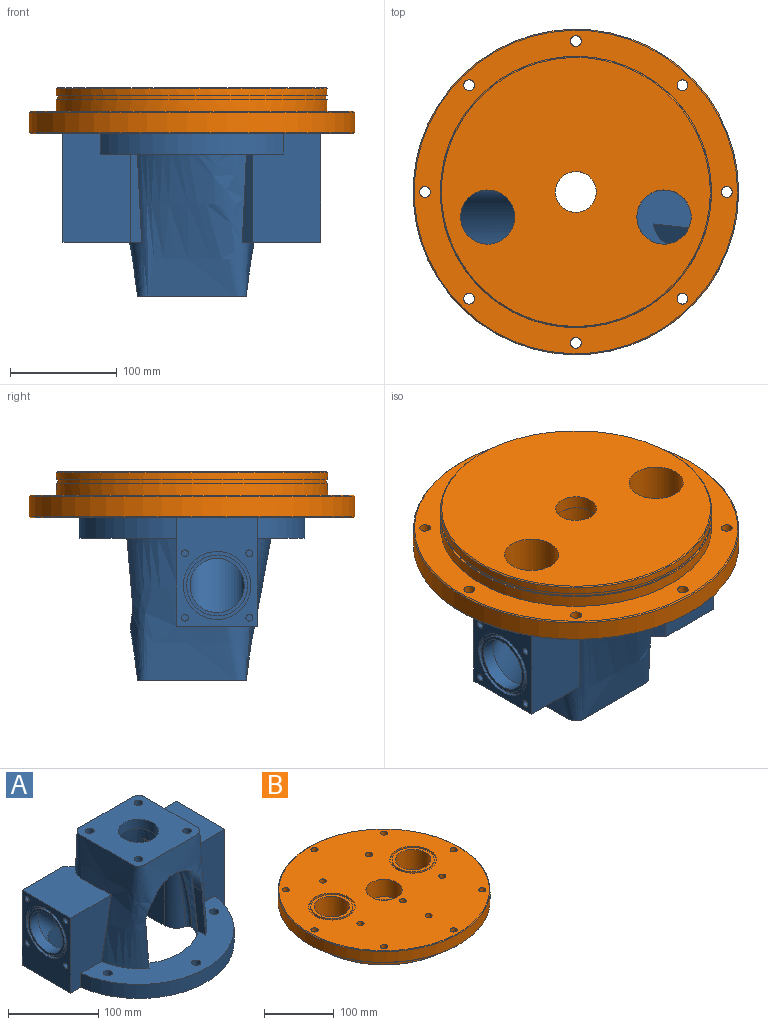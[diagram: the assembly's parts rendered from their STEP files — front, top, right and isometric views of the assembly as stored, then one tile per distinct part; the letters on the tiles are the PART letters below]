
ASSEMBLY  parts=2 mates=1
PART A: 80 faces, bbox 288x215.9x173.7 mm
  f0: plane 57.15x57.15mm, normal (-1,0,0), area 538.4mm2, adj f35,f61
  f1: plane 57.15x57.15mm, normal (1,0,0), area 538.4mm2, adj f32,f50
  f2: bspline ~71.66x6.17mm, area 502.3mm2, adj f5,f39,f43,f49
  f3: bspline ~71.51x6.17mm, area 502.2mm2, adj f5,f39,f47,f49
  f4: bspline ~70.49x6.09mm, area 502.2mm2, adj f5,f39,f45,f47
  f5: bspline ~135.38x133.3mm, area 27669.4mm2, adj f2,f3,f4,f8,f10,f16,f25,f36
  f6: bspline ~148.37x148.36mm, area 36449.8mm2, adj f7,f11,f14,f17,f19,f23,f25,f36
  f7: plane 102.6x102.6mm, normal (0,0,1), area 8407.7mm2, adj f6,f41,f43,f45,f47,f49
  f8: plane 241.5x211.66mm, normal (0,0,-1), area 21781.5mm2, adj f5,f9,f12,f13,f14,f15,f18,f19
  f9: plane 101.6x42.87mm, normal (1,0,0), area 3816.2mm2, adj f8,f10,f73,f77
  f10: plane 47.41x5.72mm, normal (0,0,1), area 156.2mm2, adj f5,f9,f73,f75,f77
  f11: plane 76.2x73.66mm, normal (0,0,1), area 4901.7mm2, adj f6,f12,f13,f14,f78
  f12: plane 101.6x76.2mm, normal (-1,0,0), area 4448.3mm2, adj f8,f11,f13,f14,f62,f64,f66,f68
  f13: plane 101.6x63.5mm, normal (0,1,0), area 5904mm2, adj f8,f11,f12,f23,f24,f78
  f14: plane 101.6x63.58mm, normal (0,-1,0), area 4926.1mm2, adj f6,f8,f11,f12,f25,f29
  f15: plane 101.61x42.87mm, normal (-1,0,0), area 3815.6mm2, adj f8,f16,f72,f76
  f16: plane 46.46x4.91mm, normal (0,0,1), area 109.2mm2, adj f5,f15,f72,f74,f76
  f17: plane 76.2x73.44mm, normal (0,0,1), area 4964.8mm2, adj f6,f18,f19,f20,f79
  f18: plane 101.6x76.2mm, normal (1,0,0), area 4448.3mm2, adj f8,f17,f19,f20,f51,f53,f55,f57
  f19: plane 101.6x62.34mm, normal (0,-1,0), area 4784.4mm2, adj f6,f8,f17,f18,f25,f29
  f20: plane 101.6x63.5mm, normal (0,1,0), area 5904mm2, adj f8,f17,f18,f23,f24,f79
  f21: cylinder r=5.08mm len=19.05mm, axis (0,0,-1), area 608mm2, adj f8,f23
  f22: cylinder r=5.08mm len=19.05mm, axis (0,0,-1), area 608mm2, adj f8,f23
  f23: plane 172.09x50.48mm, normal (0,0,1), area 4483.9mm2, adj f6,f13,f20,f21,f22,f24,f78,f79
  f24: cylinder r=105.73mm len=171.79mm, axis (0,0,-1), area 3819.9mm2, adj f8,f13,f20,f23
  f25: plane 209.44x91.19mm, normal (0,0,1), area 8522.5mm2, adj f5,f6,f14,f19,f26,f27,f28,f29
  f26: cylinder r=5.08mm len=19.05mm, axis (0,0,-1), area 608mm2, adj f8,f25
  f27: cylinder r=5.08mm len=19.05mm, axis (0,0,-1), area 608mm2, adj f8,f25
  f28: cylinder r=5.08mm len=19.05mm, axis (0,0,-1), area 608mm2, adj f8,f25
  f29: cylinder r=105.73mm len=209.44mm, axis (0,0,-1), area 5771.3mm2, adj f8,f14,f19,f25
  f30: cylinder r=25.4mm len=50.8mm, axis (0,0,1), area 6080.5mm2, adj f8,f31
  f31: torus R=25.4mm, axis (0,1,0), area 6367.5mm2, adj f30,f32
  f32: cylinder r=25.4mm len=50.8mm, axis (1,0,0), area 2026.8mm2, adj f1,f31
  f33: cylinder r=25.4mm len=50.8mm, axis (0,0,1), area 6080.5mm2, adj f8,f34
  f34: torus R=25.4mm, axis (0,-1,0), area 6367.5mm2, adj f33,f35
  f35: cylinder r=25.4mm len=50.8mm, axis (-1,0,0), area 2026.8mm2, adj f0,f34
  f36: cylinder r=44.45mm len=88.9mm, axis (0,1,0), area 1801mm2, adj f5,f6,f37,f38
  f37: plane 61.33x23.79mm, normal (-1,0,0), area 744.4mm2, adj f5,f6,f25,f36
  f38: plane 61.55x24.54mm, normal (1,0,0), area 785.2mm2, adj f5,f6,f25,f36
  f39: plane 75.87x75.87mm, normal (0,0,-1), area 4072.4mm2, adj f2,f3,f4,f40,f41,f43,f45,f47
  f40: bspline ~71.39x6.15mm, area 502.1mm2, adj f5,f39,f43,f45
  f41: cylinder r=22.23mm len=44.45mm, axis (0,0,1), area 1773.5mm2, adj f7,f39
  f42: plane 7.23x6.72mm, normal (0,0,1), area 17.3mm2, adj f5,f43
  f43: cylinder r=4.76mm len=25.4mm, axis (0,0,1), area 558.9mm2, adj f2,f5,f7,f39,f40,f42
  f44: plane 7.23x6.72mm, normal (0,0,1), area 17.3mm2, adj f5,f45
  f45: cylinder r=4.76mm len=25.4mm, axis (0,0,1), area 558.9mm2, adj f4,f5,f7,f39,f40,f44
  f46: plane 7.23x6.72mm, normal (0,0,1), area 17.3mm2, adj f5,f47
  f47: cylinder r=4.76mm len=25.4mm, axis (0,0,1), area 558.9mm2, adj f3,f4,f5,f7,f39,f46
  f48: plane 7.23x6.72mm, normal (0,0,1), area 17.3mm2, adj f5,f49
  f49: cylinder r=4.76mm len=25.4mm, axis (0,0,1), area 558.9mm2, adj f2,f3,f5,f7,f39,f48
  f50: cylinder r=28.57mm len=57.15mm, axis (1,0,0), area 513mm2, adj f1,f52
  f51: cylinder r=31.75mm len=63.5mm, axis (1,0,0), area 570mm2, adj f18,f52
  f52: plane 63.5x63.5mm, normal (1,0,0), area 601.7mm2, adj f50,f51
  f53: cylinder r=3.17mm len=12.7mm, axis (1,0,0), area 253.4mm2, adj f18,f54
  f54: plane 6.35x6.35mm, normal (1,0,0), area 31.7mm2, adj f53
  f55: cylinder r=3.17mm len=12.7mm, axis (1,0,0), area 253.4mm2, adj f18,f56
  f56: plane 6.35x6.35mm, normal (1,0,0), area 31.7mm2, adj f55
  f57: cylinder r=3.17mm len=12.7mm, axis (1,0,0), area 253.4mm2, adj f18,f58
  f58: plane 6.35x6.35mm, normal (1,0,0), area 31.7mm2, adj f57
  f59: cylinder r=3.17mm len=12.7mm, axis (1,0,0), area 253.4mm2, adj f18,f60
  f60: plane 6.35x6.35mm, normal (1,0,0), area 31.7mm2, adj f59
  f61: cylinder r=28.57mm len=57.15mm, axis (-1,0,0), area 513mm2, adj f0,f63
  f62: cylinder r=31.75mm len=63.5mm, axis (-1,0,0), area 570mm2, adj f12,f63
  f63: plane 63.5x63.5mm, normal (-1,0,0), area 601.7mm2, adj f61,f62
  f64: cylinder r=3.17mm len=12.7mm, axis (-1,0,0), area 253.4mm2, adj f12,f65
  f65: plane 6.35x6.35mm, normal (-1,0,0), area 31.7mm2, adj f64
  f66: cylinder r=3.17mm len=12.7mm, axis (-1,0,0), area 253.4mm2, adj f12,f67
  f67: plane 6.35x6.35mm, normal (-1,0,0), area 31.7mm2, adj f66
  f68: cylinder r=3.17mm len=12.7mm, axis (-1,0,0), area 253.4mm2, adj f12,f69
  f69: plane 6.35x6.35mm, normal (-1,0,0), area 31.7mm2, adj f68
  f70: cylinder r=3.17mm len=12.7mm, axis (-1,0,0), area 253.4mm2, adj f12,f71
  f71: plane 6.35x6.35mm, normal (-1,0,0), area 31.7mm2, adj f70
  f72: cylinder r=19.05mm len=101.6mm, axis (0,0,1), area 1900.4mm2, adj f8,f15,f16,f74
  f73: cylinder r=19.05mm len=101.6mm, axis (0,0,1), area 1846.6mm2, adj f8,f9,f10,f75
  f74: bspline ~108.24x18.13mm, area 649.3mm2, adj f5,f8,f16,f72
  f75: bspline ~109.03x18.64mm, area 638.6mm2, adj f5,f8,f10,f73
  f76: bspline ~104.15x16.55mm, area 408.7mm2, adj f5,f8,f15,f16
  f77: bspline ~106.89x16.35mm, area 439.2mm2, adj f5,f8,f9,f10
  f78: plane 82.55x10.16mm, normal (0.71,0.71,0), area 946.7mm2, adj f6,f11,f13,f23
  f79: plane 82.55x9.94mm, normal (-0.71,0.71,0), area 931.6mm2, adj f6,f17,f20,f23
PART B: 45 faces, bbox 304.8x304.8x43.2 mm
  f0: plane 302.77x302.77mm, normal (0,0,1), area 61705.2mm2, adj f8,f11,f13,f15,f17,f19,f21,f27
  f1: plane 60.33x60.33mm, normal (0,0,1), area 831.3mm2, adj f29,f32
  f2: plane 60.33x60.33mm, normal (0,0,1), area 831.3mm2, adj f30,f34
  f3: plane 251.84x251.84mm, normal (0,0,-1), area 44611.6mm2, adj f10,f26,f29,f30
  f4: cylinder r=126.94mm len=253.87mm, axis (0,0,-1), area 8812.3mm2, adj f7,f24
  f5: cylinder r=152.4mm len=304.8mm, axis (0,0,-1), area 18119.9mm2, adj f27,f28
  f6: cylinder r=126.94mm len=253.87mm, axis (0,0,-1), area 5469.7mm2, adj f25,f26
  f7: plane 302.77x302.77mm, normal (0,0,-1), area 20727.6mm2, adj f4,f28,f37,f38,f39,f40,f41,f42
  f8: cylinder r=26.04mm len=52.07mm, axis (0,0,1), area 4986mm2, adj f0,f9
  f9: plane 52.07x52.07mm, normal (0,0,1), area 981.7mm2, adj f8,f10
  f10: cylinder r=19.11mm len=38.23mm, axis (0,0,1), area 1525.2mm2, adj f3,f9
  f11: cylinder r=5.08mm len=19.05mm, axis (0,0,1), area 608mm2, adj f0,f12
  f12: plane 10.16x10.16mm, normal (0,0,1), area 81.1mm2, adj f11
  f13: cylinder r=5.08mm len=19.05mm, axis (0,0,1), area 608mm2, adj f0,f14
  f14: plane 10.16x10.16mm, normal (0,0,1), area 81.1mm2, adj f13
  f15: cylinder r=5.08mm len=19.05mm, axis (0,0,1), area 608mm2, adj f0,f16
  f16: plane 10.16x10.16mm, normal (0,0,1), area 81.1mm2, adj f15
  f17: cylinder r=5.08mm len=19.05mm, axis (0,0,1), area 608mm2, adj f0,f18
  f18: plane 10.16x10.16mm, normal (0,0,1), area 81.1mm2, adj f17
  f19: cylinder r=5.08mm len=19.05mm, axis (0,0,1), area 608mm2, adj f0,f20
  f20: plane 10.16x10.16mm, normal (0,0,1), area 81.1mm2, adj f19
  f21: cylinder r=4.76mm len=19.05mm, axis (0,0,1), area 570mm2, adj f0,f22
  f22: plane 9.53x9.53mm, normal (0,0,1), area 71.3mm2, adj f21
  f23: cylinder r=125.57mm len=251.14mm, axis (0,0,-1), area 2605.2mm2, adj f24,f25
  f24: plane 253.87x253.87mm, normal (0,0,-1), area 1083mm2, adj f4,f23
  f25: plane 253.87x253.87mm, normal (0,0,1), area 1083mm2, adj f6,f23
  f26: cone r=126.94mm half-angle=45deg, axis (0,0,1), area 1141.4mm2, adj f3,f6
  f27: cone r=151.38mm half-angle=45deg, axis (0,0,-1), area 1371.3mm2, adj f0,f5
  f28: cone r=152.4mm half-angle=45deg, axis (0,0,1), area 1371.3mm2, adj f5,f7
  f29: cylinder r=25.4mm len=50.8mm, axis (0,0,1), area 6891.2mm2, adj f1,f3
  f30: cylinder r=25.4mm len=50.8mm, axis (0,0,1), area 6891.2mm2, adj f2,f3
  f31: cylinder r=33.46mm len=66.93mm, axis (0,0,1), area 600.8mm2, adj f0,f33
  f32: cylinder r=30.16mm len=60.33mm, axis (0,0,1), area 541.5mm2, adj f1,f33
  f33: plane 66.93x66.93mm, normal (0,0,1), area 660mm2, adj f31,f32
  f34: cylinder r=30.16mm len=60.33mm, axis (0,0,1), area 541.5mm2, adj f2,f36
  f35: cylinder r=33.46mm len=66.93mm, axis (0,0,1), area 600.8mm2, adj f0,f36
  f36: plane 66.93x66.93mm, normal (0,0,1), area 660mm2, adj f34,f35
  f37: cylinder r=5.08mm len=20.96mm, axis (0,0,1), area 668.9mm2, adj f0,f7
  f38: cylinder r=5.08mm len=20.96mm, axis (0,0,1), area 668.9mm2, adj f0,f7
  f39: cylinder r=5.08mm len=20.96mm, axis (0,0,1), area 668.9mm2, adj f0,f7
  f40: cylinder r=5.08mm len=20.96mm, axis (0,0,1), area 668.9mm2, adj f0,f7
  f41: cylinder r=5.08mm len=20.96mm, axis (0,0,1), area 668.9mm2, adj f0,f7
  f42: cylinder r=5.08mm len=20.96mm, axis (0,0,1), area 668.9mm2, adj f0,f7
  f43: cylinder r=5.08mm len=20.96mm, axis (0,0,1), area 668.9mm2, adj f0,f7
  f44: cylinder r=5.08mm len=20.96mm, axis (0,0,1), area 668.9mm2, adj f0,f7
PLACE A rot(axis=(1,0,0),180deg) t=(26.04,35.22,77.27)mm
PLACE B rot(axis=(1,0,0),180deg) t=(26.04,35.22,77.27)mm
MATE fastened A.f24 <-> B.f8  axis (0,0,1) through (26.04,35.22,34.09)mm
